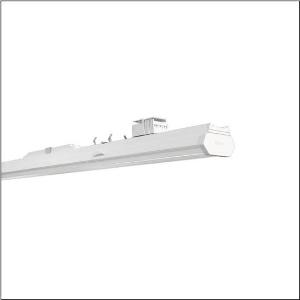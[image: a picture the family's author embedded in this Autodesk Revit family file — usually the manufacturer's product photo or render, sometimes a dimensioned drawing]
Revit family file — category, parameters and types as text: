
# Revit family: licross_21_protected_ho_52td12mn4e5m
name_source: partatom
category: Lighting Fixtures
units: mm (PartAtom-declared; Revit-internal decimal feet)

## family parameters
Cut with Voids When Loaded = No
Host = Face
Light Source = No
Part Type = Normal
Room Calculation Point = No
Round Connector Dimension = Use Diameter
Shared = No

## types (1)
- --- (1 x LED, 14780 lm, 83.2 W, 4000K)
    Apparent Load = 83 VA
    CIE Flux Codes = 70 91 97 98 100
    Color Rendering = 80
    Color Temperature = 4000K
    Default Elevation = 1800 mm
    Description = Licross 21 Protected HO, luminaire insert, of sheet steel, galvanised, coil coated, white, length: 1.500mm, width: 90mm, height: 101mm, LED rated luminous flux: 14.790lm, light colour: 840, SDCM (Standard Deviation of Colour Matching)MacAdam ≤ 3 SDCM (initial), control gear: ON/OFF Multilumen, with plug, 3-pole, with phase selection, mains connection: 220..240V, AC, 50/60Hz, rated input power: 83W, internal wiring halogen-free, primary light control with lens, of plastic, primary optical cover: cover, of PMMA, light emission: direct distribution, primary light characteristic: symmetric, protection rating (complete): IP54, insulation class (complete): insulation class I (protective earthing), certification: CE, ENEC, VDE, UKCA, protection symbol: D if used in an environment with non-conductive dust loads with corresponding accessories, impact resistance: IK06, permissible ambient temperature for indoor applications: -35..+35°C, corresponds to IFS (International Featured Standards) requirements for safety and quality in the food industry, reducing of maximum allowable ambient temperature of 5°C with ceiling mounting, LABS conformity tested according to VDMA 24364:2018-05, The light source and the operating device comply with the requirements of the Ecodesign Regulation (EU) 2019/2020 and are replaceable in accordance with this regulation, packaging unit: 1 piece
    Height = 92 mm
    Lamp = 1 x LED
    Lamp Light Flux = 14780 lm
    Lamp Power = 83.2 W
    Lamp count = 1
    Length = 1500 mm
    Luminous efficacy = 178 lm/W
    Manufacturer = Siteco
    ModVariant = No
    Model = 52TD12MN4E5M
    Mounting Place = Ceiling
    Mounting Type = Pendant
    Number of Poles = 1
    OnlyDefault = Yes
    Power Factor = 1
    Product Name = Licross 21 Protected HO
    Product group = luminaire insert | ceiling pendant
    ProductGroupID = 901
    Protection Class = Protection class I
    Protection Degree = IP 54
    RLX_Detail_Level = 1
    RLX_Emergency_Light_Flux = 0 lm
    RLX_Emergency_Type = 0
    RLX_Emergency_Type_DB = No
    RlxData = <blob elided: 22341 chars, md5=1077e046>
    Socket = socket
    Standby Power = 0 W
    System Light Flux = 14780 lm
    System Power = 83 W
    Type Comments = factory setting: luminous flux: 100 % | (A | C | E) | 195 mA
    Type Image = l_1256148.jpg
    URL = http://relux.com
    VarID = @adj_110675
    Voltage = 0 V
    Weight = 0.00 kg
    Width = 88 mm

## geometry (parser evidence)
native form markers: Blend x4, Sweep x10
no freeform markers — native parametric forms only
